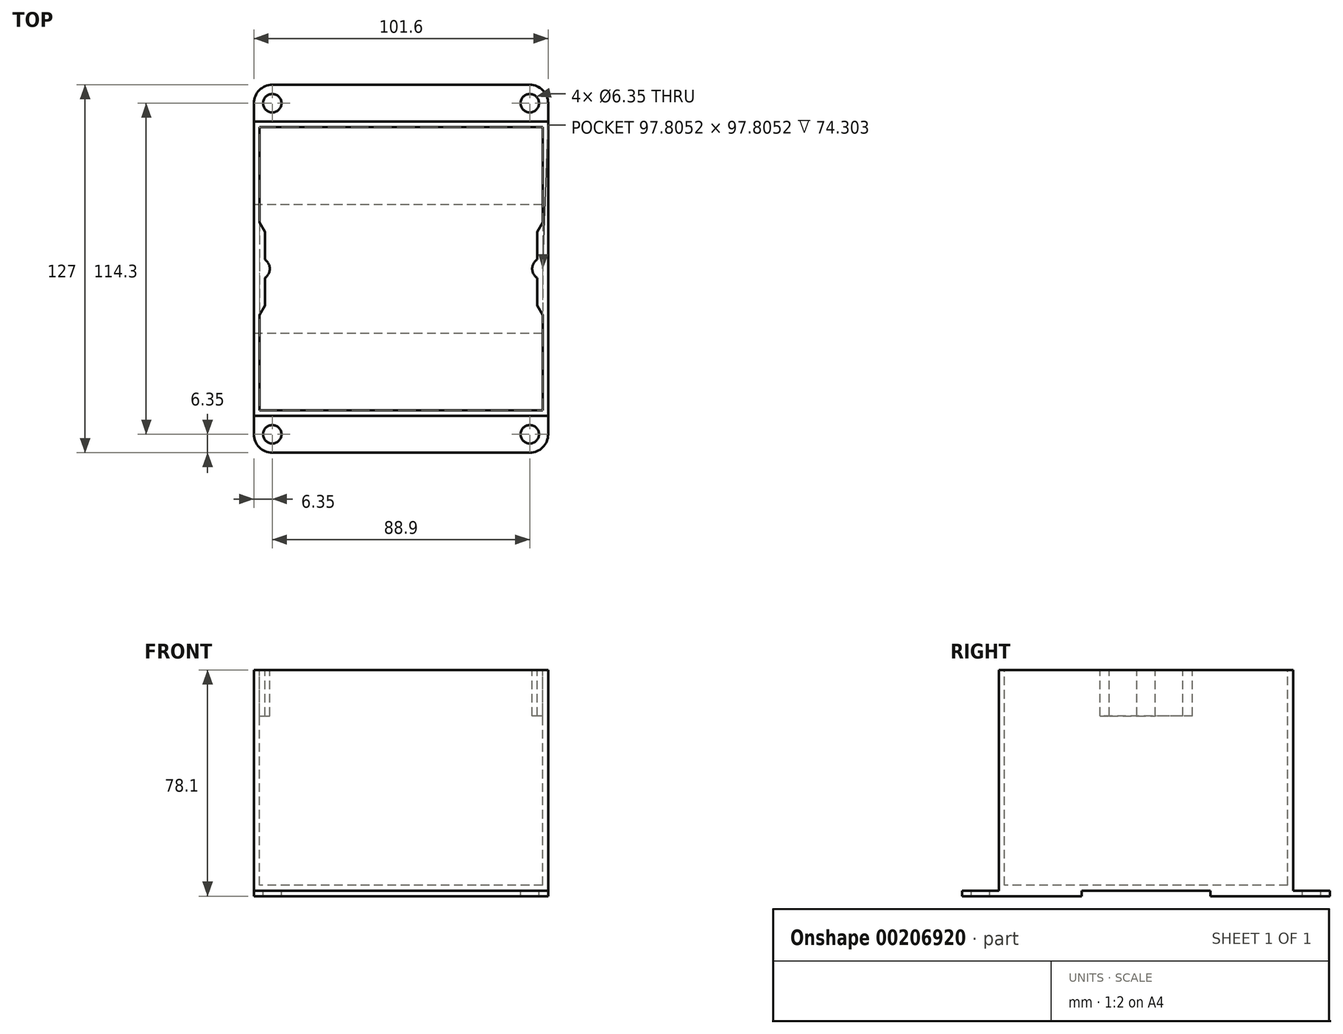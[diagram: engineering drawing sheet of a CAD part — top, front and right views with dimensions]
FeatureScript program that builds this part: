
annotation { "Feature Type Name" : "Feature", "Feature Type Description" : "" }
export const myFeature = defineFeature(function(context is Context, id is Id, definition is map)
    precondition{}
    {
        {
            var Q0;
            Q0=qCreatedBy(makeId("Top.planeOp"),FACE);
            var sketch = newSketch(context, id + "F0", { "sketchPlane" : qUnion([Q0])});
            skLineSegment(sketch, "E0.bottom", {"start": v(-50.8, 50.8) * mm, "end": v(50.8, 50.8) * mm});
            skLineSegment(sketch, "E0.top", {"start": v(-50.8, -50.8) * mm, "end": v(50.8, -50.8) * mm});
            skLineSegment(sketch, "E0.left", {"start": v(-50.8, 50.8) * mm, "end": v(-50.8, -50.8) * mm});
            skLineSegment(sketch, "E0.right", {"start": v(50.8, 50.8) * mm, "end": v(50.8, -50.8) * mm});
            skPoint(sketch, "E0.middle", {"position": v(0, 0) * mm});
            skSolve(sketch);
        }
        {
            var Q0;
            Q0=qSketchRegion(id+"F0",true);
            extrude(context, id + "F1", {"entities" : qUnion([Q0]), "depth" : 76.2 * mm});
        }
        {
            var Q0;
            Q0=makeQuery(id+"F1.opExtrude","CAP_FACE",FACE,{"disambiguationData":[OSD([sQuery(id+"F0.wireOp",EDGE,"E0.bottom"),sQuery(id+"F0.wireOp",EDGE,"E0.top"),sQuery(id+"F0.wireOp",EDGE,"E0.left"),sQuery(id+"F0.wireOp",EDGE,"E0.right")])],"isStart":false});
            var sketch = newSketch(context, id + "F2", { "sketchPlane" : qUnion([Q0])});
            skLineSegment(sketch, "E1.bottom", {"start": v(48.9, 48.9) * mm, "end": v(-48.9, 48.9) * mm});
            skLineSegment(sketch, "E1.top", {"start": v(48.9, -48.9) * mm, "end": v(-48.9, -48.9) * mm});
            skLineSegment(sketch, "E1.left", {"start": v(48.9, 48.9) * mm, "end": v(48.9, -48.9) * mm});
            skLineSegment(sketch, "E1.right", {"start": v(-48.9, 48.9) * mm, "end": v(-48.9, -48.9) * mm});
            skPoint(sketch, "E1.middle", {"position": v(0, 0) * mm});
            skSolve(sketch);
        }
        {
            var Q0;
            Q0=qSketchRegion(id+"F2",true);
            extrude(context, id + "F3", {"entities" : qUnion([Q0]), "operationType" : NewBodyOperationType.REMOVE, "oppositeDirection" : true, "depth" : 74.3 * mm});
        }
        {
            var Q0;
            Q0=makeQuery(id+"F1.opExtrude","CAP_FACE",FACE,{"disambiguationData":[OSD([sQuery(id+"F0.wireOp",EDGE,"E0.bottom"),sQuery(id+"F0.wireOp",EDGE,"E0.top"),sQuery(id+"F0.wireOp",EDGE,"E0.left"),sQuery(id+"F0.wireOp",EDGE,"E0.right")])],"isStart":false});
            var sketch = newSketch(context, id + "F4", { "sketchPlane" : qUnion([Q0])});
            skLineSegment(sketch, "E2", {"start": v(-48.9, 15.99) * mm, "end": v(-47, 12.7) * mm});
            skLineSegment(sketch, "E3", {"start": v(-47, 12.7) * mm, "end": v(-47, 3.17) * mm});
            skLineSegment(sketch, "E4", {"start": v(-48.9, -15.99) * mm, "end": v(-47, -12.7) * mm});
            skLineSegment(sketch, "E5", {"start": v(-47, -12.7) * mm, "end": v(-47, -3.18) * mm});
            skLineSegment(sketch, "E6", {"start": v(48.9, 15.99) * mm, "end": v(47, 12.7) * mm});
            skLineSegment(sketch, "E7", {"start": v(47, 12.7) * mm, "end": v(47, 3.18) * mm});
            skLineSegment(sketch, "E8", {"start": v(48.9, -15.99) * mm, "end": v(47, -12.7) * mm});
            skLineSegment(sketch, "E9", {"start": v(47, -12.7) * mm, "end": v(47, -3.17) * mm});
            skArc(sketch, "E10", {"start": v(-47, -3.18) * mm, "mid": v(-45.3, 0) * mm, "end": v(-47, 3.17) * mm});
            skArc(sketch, "E11", {"start": v(47, 3.18) * mm, "mid": v(45.3, 0) * mm, "end": v(47, -3.17) * mm});
            skLineSegment(sketch, "E12", {"start": v(-48.9, -15.99) * mm, "end": v(-48.9, 15.99) * mm});
            skLineSegment(sketch, "E13", {"start": v(48.9, -15.99) * mm, "end": v(48.9, 15.99) * mm});
            skSolve(sketch);
        }
        {
            var Q0;
            Q0=qSketchRegion(id+"F4",true);
            extrude(context, id + "F5", {"entities" : qUnion([Q0]), "operationType" : NewBodyOperationType.ADD, "oppositeDirection" : true, "depth" : 15.88 * mm});
        }
        {
            var Q0;
            Q0=makeQuery(id+"F1.opExtrude","CAP_FACE",FACE,{"disambiguationData":[OSD([sQuery(id+"F0.wireOp",EDGE,"E0.bottom"),sQuery(id+"F0.wireOp",EDGE,"E0.top"),sQuery(id+"F0.wireOp",EDGE,"E0.left"),sQuery(id+"F0.wireOp",EDGE,"E0.right")])],"isStart":true});
            var sketch = newSketch(context, id + "F6", { "sketchPlane" : qUnion([Q0])});
            skLineSegment(sketch, "E14", {"start": v(-50.8, 22.23) * mm, "end": v(50.8, 22.23) * mm});
            skLineSegment(sketch, "E15", {"start": v(50.8, 22.23) * mm, "end": v(50.8, 57.15) * mm});
            skLineSegment(sketch, "E16", {"start": v(44.45, 63.5) * mm, "end": v(-44.45, 63.5) * mm});
            skLineSegment(sketch, "E17", {"start": v(-50.8, 57.15) * mm, "end": v(-50.8, 22.23) * mm});
            skPoint(sketch, "E18.visualSharp", {"position": v(-50.8, 63.5) * mm});
            skArc(sketch, "E18.filletArc", {"start": v(-44.45, 63.5) * mm, "mid": v(-48.94, 61.64) * mm, "end": v(-50.8, 57.15) * mm});
            skPoint(sketch, "E19.visualSharp", {"position": v(50.8, 63.5) * mm});
            skArc(sketch, "E19.filletArc", {"start": v(50.8, 57.15) * mm, "mid": v(48.94, 61.64) * mm, "end": v(44.45, 63.5) * mm});
            skCircle(sketch, "E20", {"center": v(-44.45, 57.15) * mm, "radius": 3.18 * mm});
            skCircle(sketch, "E21", {"center": v(44.45, 57.15) * mm, "radius": 3.18 * mm});
            skLineSegment(sketch, "E22", {"start": v(-61.36, 0) * mm, "end": v(78.94, 0) * mm});
            skLineSegment(sketch, "E23.MirrorCS", {"start": v(-50.8, -22.23) * mm, "end": v(50.8, -22.23) * mm});
            skLineSegment(sketch, "E24.MirrorCS", {"start": v(-50.8, -57.15) * mm, "end": v(-50.8, -22.23) * mm});
            skArc(sketch, "E25.MirrorCS", {"start": v(-44.45, -63.5) * mm, "mid": v(-48.94, -61.64) * mm, "end": v(-50.8, -57.15) * mm});
            skCircle(sketch, "E26.MirrorC", {"center": v(-44.45, -57.15) * mm, "radius": 3.18 * mm});
            skLineSegment(sketch, "E27.MirrorCS", {"start": v(44.45, -63.5) * mm, "end": v(-44.45, -63.5) * mm});
            skCircle(sketch, "E28.MirrorC", {"center": v(44.45, -57.15) * mm, "radius": 3.18 * mm});
            skLineSegment(sketch, "E29.MirrorCS", {"start": v(50.8, -22.23) * mm, "end": v(50.8, -57.15) * mm});
            skArc(sketch, "E30.MirrorCS", {"start": v(50.8, -57.15) * mm, "mid": v(48.94, -61.64) * mm, "end": v(44.45, -63.5) * mm});
            skSolve(sketch);
        }
        {
            var Q0;
            Q0=qSketchRegion(id+"F6",true);
            extrude(context, id + "F7", {"entities" : qUnion([Q0]), "operationType" : NewBodyOperationType.ADD, "depth" : 1.9 * mm});
        }
    });
